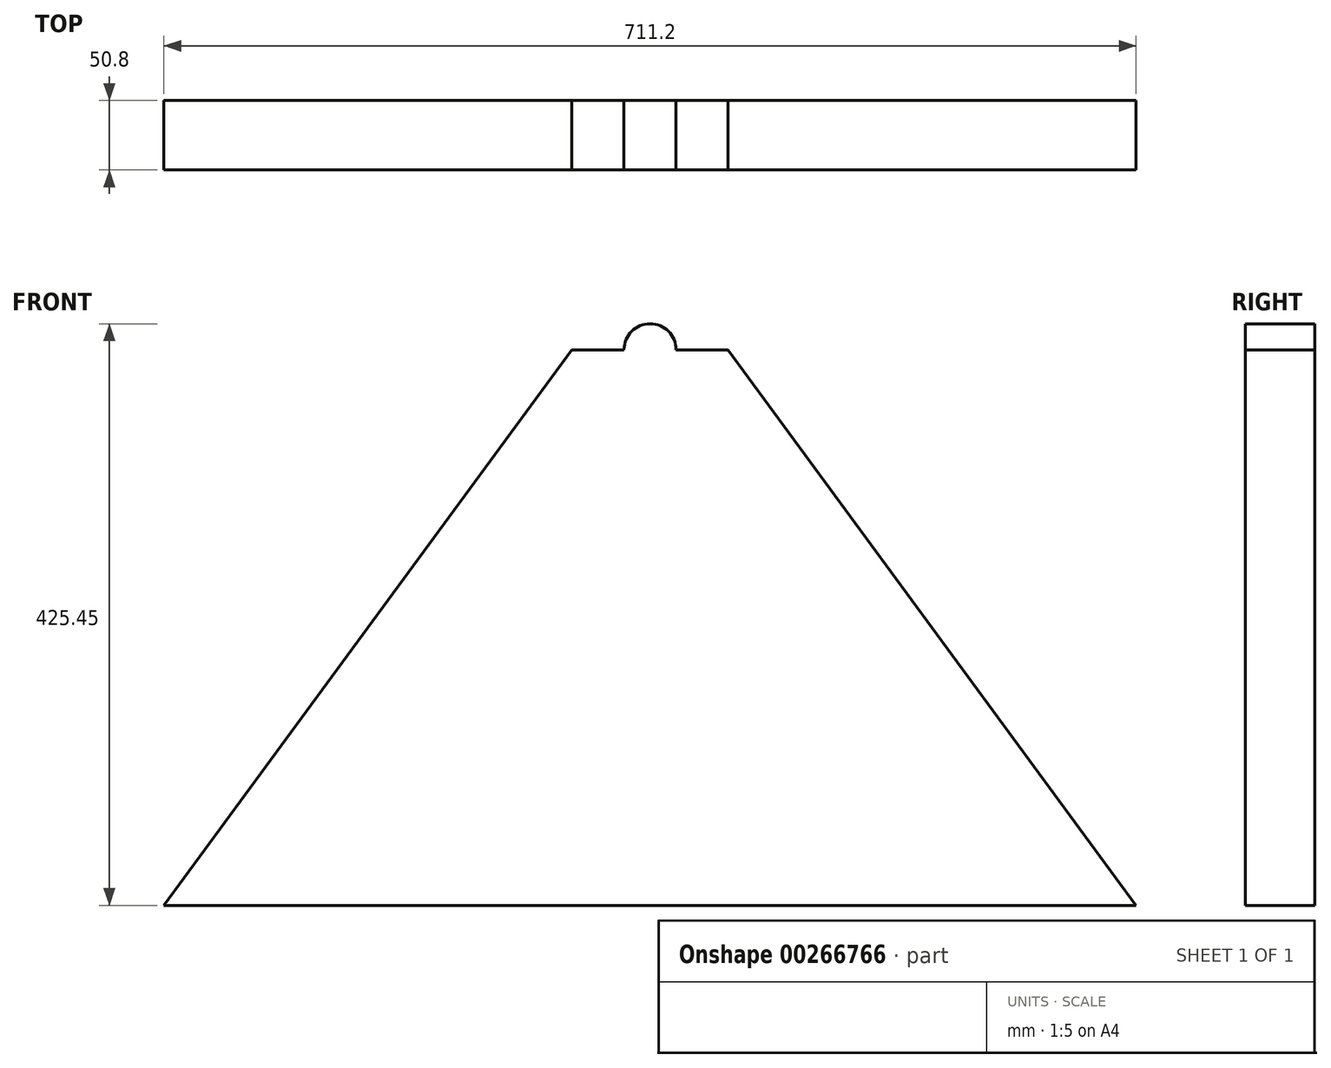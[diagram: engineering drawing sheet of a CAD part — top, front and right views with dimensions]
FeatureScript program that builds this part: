
annotation { "Feature Type Name" : "Feature", "Feature Type Description" : "" }
export const myFeature = defineFeature(function(context is Context, id is Id, definition is map)
    precondition{}
    {
        {
            var Q0;
            Q0=qCreatedBy(makeId("Front.planeOp"),FACE);
            var sketch = newSketch(context, id + "F0", { "sketchPlane" : qUnion([Q0])});
            skLineSegment(sketch, "E0", {"start": v(0, 63.5) * mm, "end": v(-57.15, 63.5) * mm});
            skLineSegment(sketch, "E1", {"start": v(-57.15, 63.5) * mm, "end": v(-355.6, -342.9) * mm});
            skLineSegment(sketch, "E2", {"start": v(-355.6, -342.9) * mm, "end": v(0, -342.9) * mm});
            skLineSegment(sketch, "E3.MirrorCS", {"start": v(355.6, -342.9) * mm, "end": v(0, -342.9) * mm});
            skLineSegment(sketch, "E4.MirrorCS", {"start": v(57.15, 63.5) * mm, "end": v(355.6, -342.9) * mm});
            skLineSegment(sketch, "E5.MirrorCS", {"start": v(0, 63.5) * mm, "end": v(57.15, 63.5) * mm});
            skLineSegment(sketch, "E6", {"start": v(57.15, 63.5) * mm, "end": v(57.15, -342.9) * mm});
            skCircle(sketch, "E7", {"center": v(0, 63.5) * mm, "radius": 19.05 * mm});
            skSolve(sketch);
        }
        {
            var Q0;
            Q0 = qSketchRegion(id + "F0", true);
            extrude(context, id + "F1", {"entities" : qUnion([Q0]), "depth" : 50.8 * mm});
        }
    });
